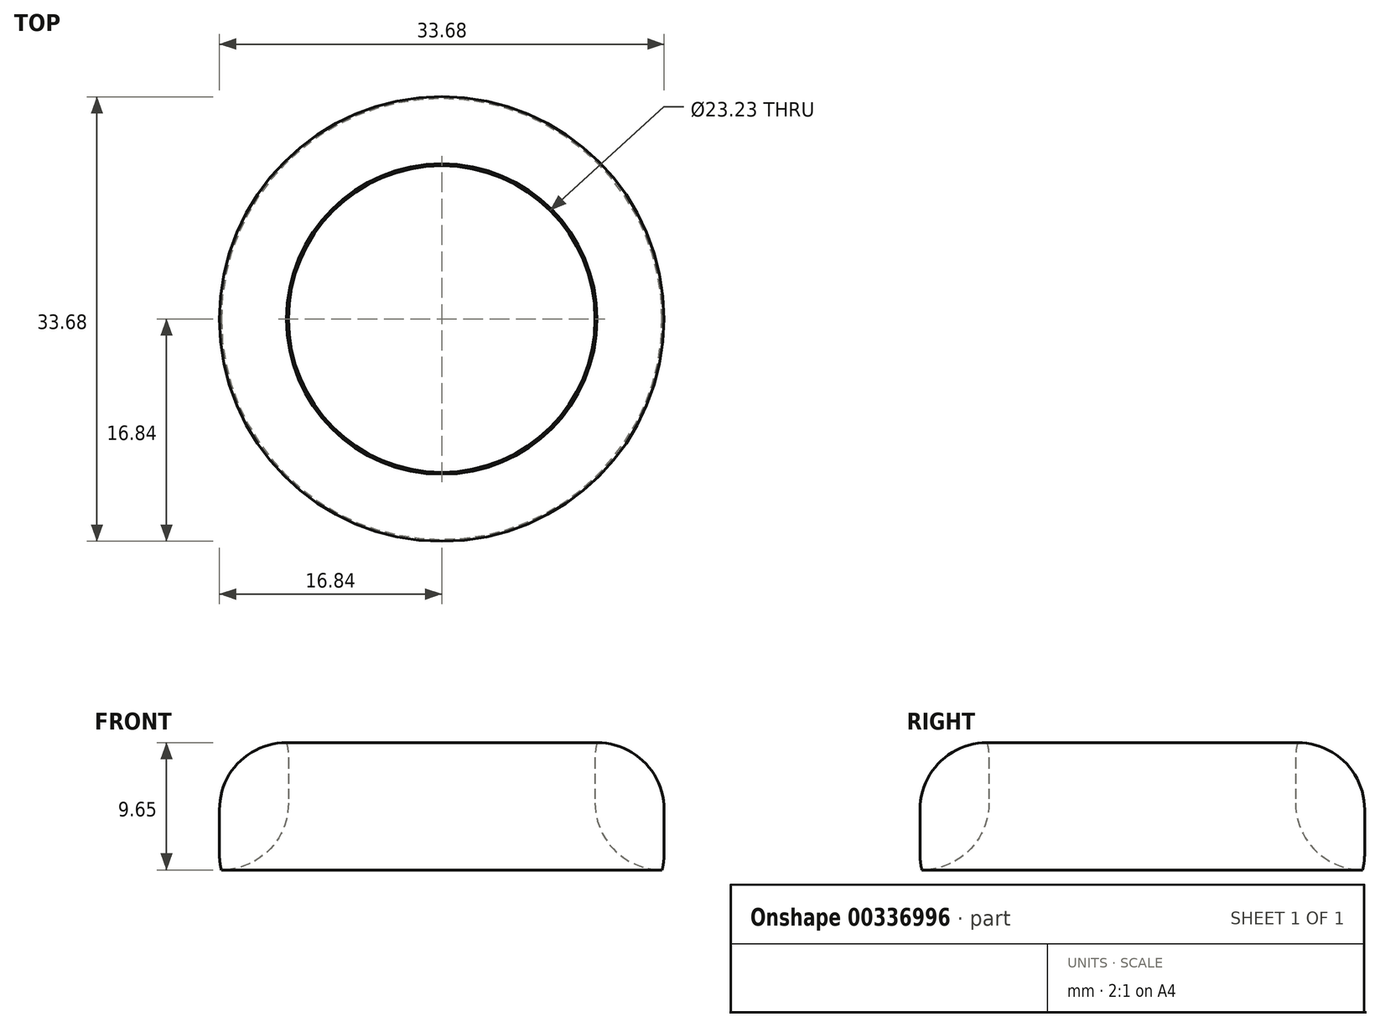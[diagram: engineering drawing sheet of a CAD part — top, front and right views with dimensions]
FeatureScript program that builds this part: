
annotation { "Feature Type Name" : "Feature", "Feature Type Description" : "" }
export const myFeature = defineFeature(function(context is Context, id is Id, definition is map)
    precondition{}
    {
        {
            var Q0;
            Q0=qCreatedBy(makeId("Top.planeOp"),FACE);
            var sketch = newSketch(context, id + "F0", { "sketchPlane" : qUnion([Q0])});
            skCircle(sketch, "E0", {"center": v(0, 0) * mm, "radius": 16.84 * mm});
            skCircle(sketch, "E1", {"center": v(0, 0) * mm, "radius": 11.62 * mm});
            skSolve(sketch);
        }
        {
            var Q0;
            Q0=makeQuery(id+"F0.imprint","IMPRINT",FACE,{"disambiguationData":[TD([[makeQuery(id+"F0.imprint","IMPRINT",EDGE,{"derivedFrom":sQuery(id+"F0.wireOp",EDGE,"E0")}),1.0]])]});
            extrude(context, id + "F1", {"entities" : qUnion([Q0]), "depth" : 9.65 * mm});
        }
        {
            var Q0;
            Q0=makeQuery(id+"F1.opExtrude","CAP_FACE",FACE,{"disambiguationData":[OSD([sQuery(id+"F0.wireOp",EDGE,"E0")])],"isStart":false});
            var sketch = newSketch(context, id + "F2", { "sketchPlane" : qUnion([Q0])});
            skSolve(sketch);
        }
        {
            var Q0;
            Q0=makeQuery(id+"F1.opExtrude","CAP_EDGE",EDGE,{"disambiguationData":[OSD([sQuery(id+"F0.wireOp",EDGE,"E0")])],"isStart":false});
            fillet(context, id + "F3", {"entities" : qUnion([Q0]), "radius" : 5.08 * mm, "tangentPropagation" : true, "allowEdgeOverflow" : false});
        }
        {
            var Q0;
            Q0=makeQuery(id+"F1.opExtrude","SWEPT_FACE",FACE,{"disambiguationData":[OSD([sQuery(id+"F0.wireOp",EDGE,"E1")])]});
            fillet(context, id + "F4", {"entities" : qUnion([Q0]), "radius" : 5.08 * mm, "tangentPropagation" : true, "allowEdgeOverflow" : false});
        }
        {
            var Q0;
            Q0=makeQuery(id+"F1.opExtrude","CAP_EDGE",EDGE,{"disambiguationData":[OSD([sQuery(id+"F0.wireOp",EDGE,"E0")])],"isStart":true});
            var Q1;
            {var subQ0=sQuery(id+"F0.wireOp",EDGE,"E1");Q1=makeQuery(id+"F4.opFillet","BLEND_EDGE",EDGE,{"blendedFrom":[makeQuery(id+"F1.opExtrude","CAP_EDGE",EDGE,{"disambiguationData":[OSD([subQ0])],"isStart":true}),makeQuery(id+"F1.opExtrude","SWEPT_FACE",FACE,{"disambiguationData":[OSD([subQ0])]})],"blendedInto":[makeQuery(id+"F1.opExtrude","SWEPT_FACE",FACE,{"disambiguationData":[OSD([subQ0])]})]});}
            var Q2;
            {var subQ0=sQuery(id+"F0.wireOp",EDGE,"E1");Q2=makeQuery(id+"F4.opFillet","BLEND_EDGE",EDGE,{"blendedFrom":[makeQuery(id+"F1.opExtrude","CAP_EDGE",EDGE,{"disambiguationData":[OSD([subQ0])],"isStart":false}),makeQuery(id+"F1.opExtrude","SWEPT_FACE",FACE,{"disambiguationData":[OSD([subQ0])]})],"blendedInto":[makeQuery(id+"F1.opExtrude","SWEPT_FACE",FACE,{"disambiguationData":[OSD([subQ0])]})]});}
            fillet(context, id + "F5", {"entities" : qUnion([Q0, Q1, Q2]), "radius" : 5.08 * mm, "tangentPropagation" : true, "allowEdgeOverflow" : false});
        }
    });
